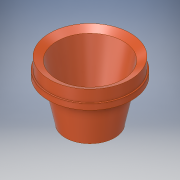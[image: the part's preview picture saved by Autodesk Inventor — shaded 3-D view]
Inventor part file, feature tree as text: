
AUTODESK INVENTOR PART (.ipt)
format: ipt  version: 2017 SP1 (Build 210196100, 196)  size: 172,032 bytes
history: native  units: in
note: dims shown in document units (in); Inventor stores cm internally (conversion verified against a paired STEP export)
features: revolve x1, sketch x1
ambient origin geometry x8: Origin, YZ Plane, XZ Plane, XY Plane, X Axis, Y Axis, Z Axis, Center Point
bodies: Body1 (feature_tree)
feature tree (2):
  revolve  "Revolution3"  [1 undecoded]
  sketch  "Sketch1"  dims[d0=1.13in d3=0.1718in d5=1.0in d6=1.0in d7=90.0deg d8=0.5in d9=15.0deg d31=0.25in d34=15.0deg d37=1.75in d40=3.75in d41=0.125in d46=0.75in d47=0.5in d51=0.5in d52=0.25in d54=0.5in d55=0.5in d56=1.25in d58=0.0017in d59=0.5in d60=0.5in d61=1.0in d62=0.234in d63=0.234in d64=0.125in d67=0.25in d68=4.25in d69=0.25in d70=0.25in d71=0.125in d73=3.4in d74=1.25in d75=0.2498in d77=90.0deg]
note: 1 required parameter value undecoded (feature->parameter linkage not recoverable at this tier; creation-order binding heuristic only, values carry confidence <= 0.55)
